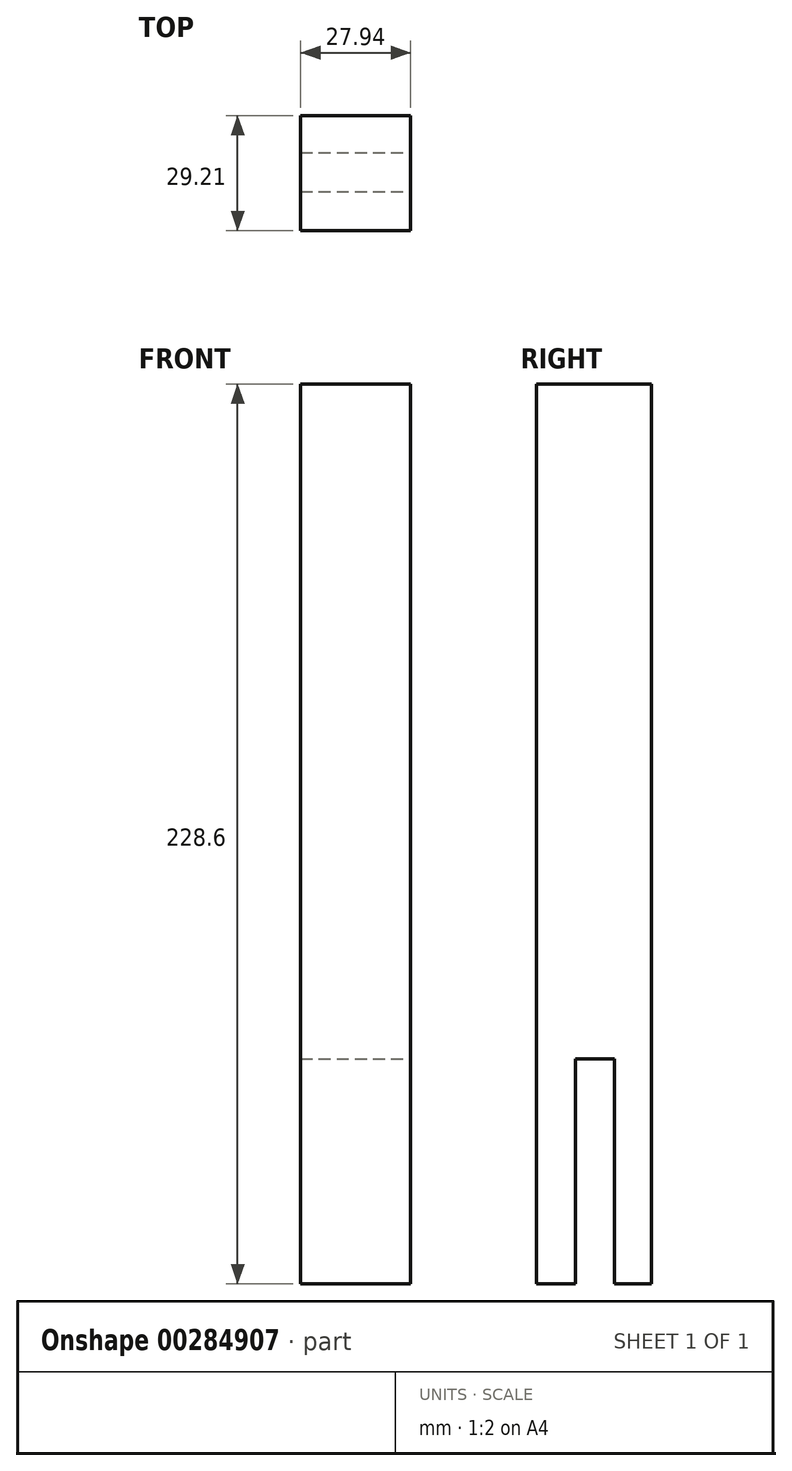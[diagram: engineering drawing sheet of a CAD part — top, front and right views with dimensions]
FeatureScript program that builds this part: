
annotation { "Feature Type Name" : "Feature", "Feature Type Description" : "" }
export const myFeature = defineFeature(function(context is Context, id is Id, definition is map)
    precondition{}
    {
        {
            var Q0;
            Q0=qCreatedBy(makeId("Right.planeOp"),FACE);
            var sketch = newSketch(context, id + "F0", { "sketchPlane" : qUnion([Q0])});
            skLineSegment(sketch, "E0.top", {"start": v(0, 228.6) * mm, "end": v(29.2, 228.6) * mm});
            skLineSegment(sketch, "E0.left", {"start": v(0, 0) * mm, "end": v(0, 228.6) * mm});
            skLineSegment(sketch, "E0.right", {"start": v(29.2, 0) * mm, "end": v(29.2, 228.6) * mm});
            skLineSegment(sketch, "E1", {"start": v(29.2, 0) * mm, "end": v(19.81, 0) * mm});
            skLineSegment(sketch, "E2", {"start": v(19.81, 0) * mm, "end": v(19.81, 57.15) * mm});
            skLineSegment(sketch, "E3", {"start": v(19.81, 57.15) * mm, "end": v(9.9, 57.15) * mm});
            skLineSegment(sketch, "E4", {"start": v(9.9, 57.15) * mm, "end": v(9.9, 0) * mm});
            skLineSegment(sketch, "E5", {"start": v(9.9, 0) * mm, "end": v(0, 0) * mm});
            skSolve(sketch);
        }
        {
            var Q0;
            Q0=makeQuery(id+"F0.imprint","IMPRINT",FACE,{"disambiguationData":[TD([[makeQuery(id+"F0.imprint","IMPRINT",EDGE,{"derivedFrom":sQuery(id+"F0.wireOp",EDGE,"E0.top")}),-1.0]])]});
            extrude(context, id + "F1", {"entities" : qUnion([Q0]), "oppositeDirection" : true, "depth" : 27.94 * mm});
        }
    });
